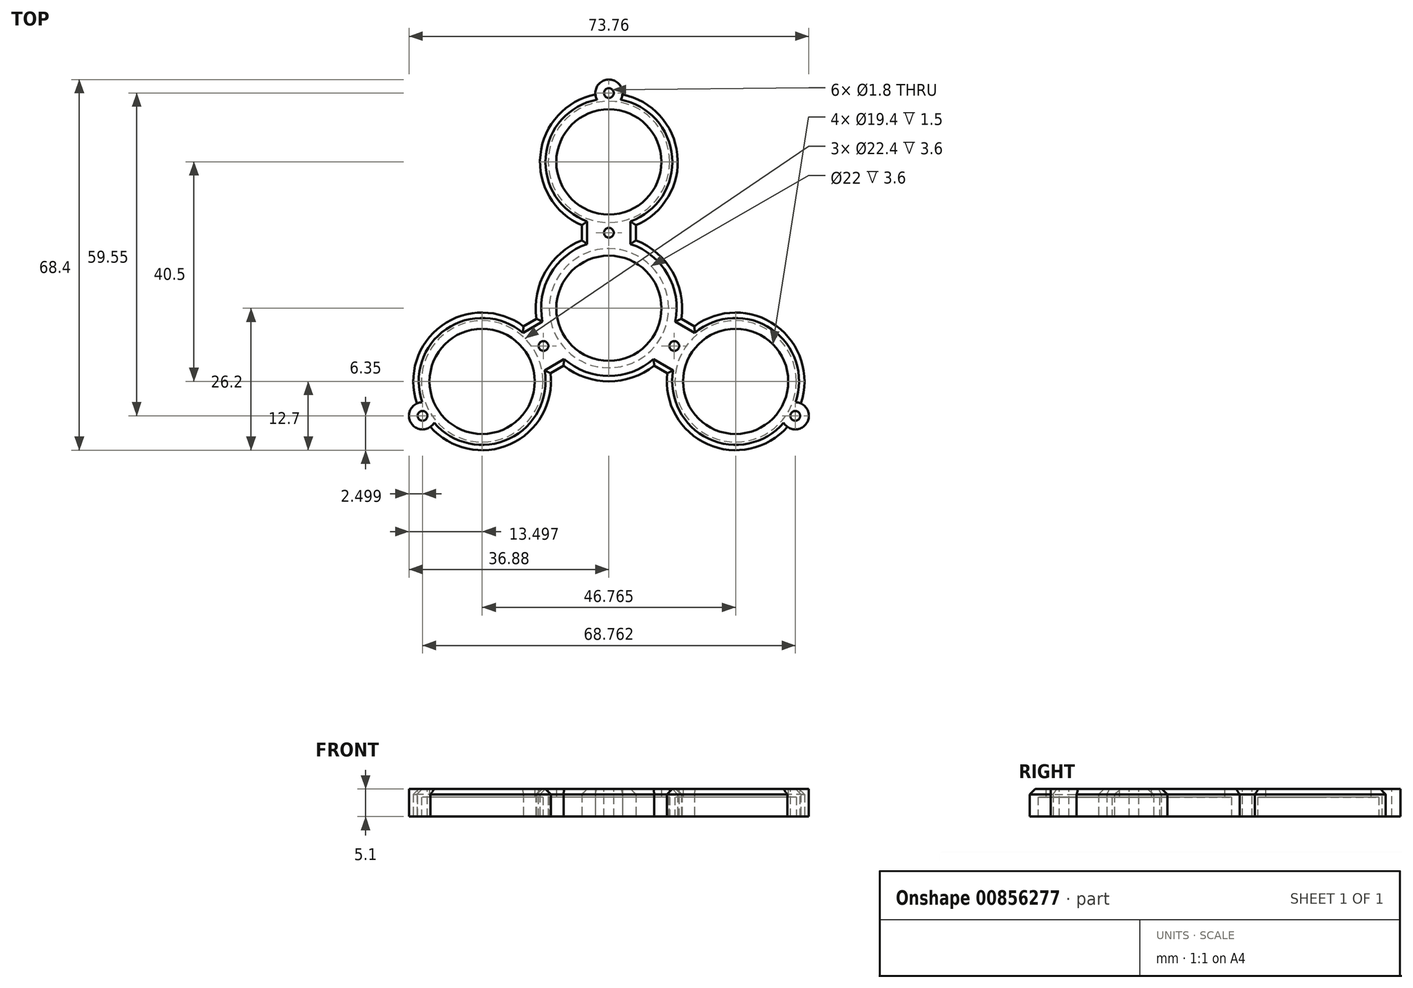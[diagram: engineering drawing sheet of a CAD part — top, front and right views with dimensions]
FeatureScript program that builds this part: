
annotation { "Feature Type Name" : "Feature", "Feature Type Description" : "" }
export const myFeature = defineFeature(function(context is Context, id is Id, definition is map)
    precondition{}
    {
        {
            var Q0;
            Q0=qCreatedBy(makeId("Top.planeOp"),FACE);
            var sketch = newSketch(context, id + "F0", { "sketchPlane" : qUnion([Q0])});
            skCircle(sketch, "E0", {"center": v(0, 0) * mm, "radius": 11 * mm});
            skCircle(sketch, "E1", {"center": v(0, 27) * mm, "radius": 11.2 * mm});
            skLineSegment(sketch, "E2", {"start": v(-5, 15.33) * mm, "end": v(-5, 12.54) * mm});
            skLineSegment(sketch, "E3", {"start": v(5, 15.33) * mm, "end": v(5, 12.54) * mm});
            skLineSegment(sketch, "E4", {"start": v(0, 27) * mm, "end": v(0, 13.5) * mm, "construction": true});
            skLineSegment(sketch, "E5", {"start": v(-5, 13.93) * mm, "end": v(0, 13.93) * mm, "construction": true});
            skLineSegment(sketch, "E6", {"start": v(0, 13.5) * mm, "end": v(0, 0) * mm, "construction": true});
            skLineSegment(sketch, "E7", {"start": v(0, 13.93) * mm, "end": v(5, 13.93) * mm, "construction": true});
            skArc(sketch, "E8", {"start": v(-2.49, 39.45) * mm, "mid": v(0, 37.2) * mm, "end": v(2.49, 39.45) * mm, "construction": true});
            skArc(sketch, "E9", {"start": v(2.49, 39.45) * mm, "mid": v(0, 42.2) * mm, "end": v(-2.49, 39.45) * mm});
            skArc(sketch, "E10", {"start": v(-2.49, 39.45) * mm, "mid": v(-12.63, 28.32) * mm, "end": v(-5, 15.33) * mm});
            skArc(sketch, "E11", {"start": v(-5, 15.33) * mm, "mid": v(0, 14.3) * mm, "end": v(5, 15.33) * mm, "construction": true});
            skArc(sketch, "E12", {"start": v(5, 15.33) * mm, "mid": v(12.63, 28.32) * mm, "end": v(2.49, 39.45) * mm});
            skArc(sketch, "E13", {"start": v(-5, 12.54) * mm, "mid": v(0, -13.5) * mm, "end": v(5, 12.54) * mm});
            skArc(sketch, "E14", {"start": v(5, 12.54) * mm, "mid": v(0, 13.5) * mm, "end": v(-5, 12.54) * mm, "construction": true});
            skArc(sketch, "E15.1.0", {"start": v(-35.41, -17.57) * mm, "mid": v(-36.55, -21.1) * mm, "end": v(-32.92, -21.88) * mm});
            skArc(sketch, "E15.1.1", {"start": v(-32.92, -21.88) * mm, "mid": v(-18.2, -25.1) * mm, "end": v(-10.77, -12) * mm});
            skLineSegment(sketch, "E15.1.2", {"start": v(-10.77, -12) * mm, "end": v(-8.36, -10.6) * mm});
            skArc(sketch, "E15.1.3", {"start": v(-15.77, -3.33) * mm, "mid": v(-30.84, -3.22) * mm, "end": v(-35.41, -17.57) * mm});
            skLineSegment(sketch, "E15.1.4", {"start": v(-15.77, -3.33) * mm, "end": v(-13.36, -1.94) * mm});
            skCircle(sketch, "E15.1.5", {"center": v(-23.38, -13.5) * mm, "radius": 11.2 * mm});
            skArc(sketch, "E15.2.0", {"start": v(32.92, -21.88) * mm, "mid": v(36.55, -21.1) * mm, "end": v(35.41, -17.57) * mm});
            skArc(sketch, "E15.2.1", {"start": v(35.41, -17.57) * mm, "mid": v(30.84, -3.22) * mm, "end": v(15.77, -3.33) * mm});
            skLineSegment(sketch, "E15.2.2", {"start": v(15.77, -3.33) * mm, "end": v(13.36, -1.94) * mm});
            skArc(sketch, "E15.2.3", {"start": v(10.77, -12) * mm, "mid": v(18.2, -25.1) * mm, "end": v(32.92, -21.88) * mm});
            skLineSegment(sketch, "E15.2.4", {"start": v(10.77, -12) * mm, "end": v(8.36, -10.6) * mm});
            skCircle(sketch, "E15.2.5", {"center": v(23.38, -13.5) * mm, "radius": 11.2 * mm});
            skSolve(sketch);
        }
        {
            var Q0;
            Q0=makeQuery(id+"F0.imprint","IMPRINT",FACE,{"disambiguationData":[TD([[makeQuery(id+"F0.imprint","IMPRINT",EDGE,{"derivedFrom":sQuery(id+"F0.wireOp",EDGE,"E0")}),-1.0]])]});
            var Q1;
            Q1=makeQuery(id+"F0.imprint","IMPRINT",FACE,{"disambiguationData":[TD([[makeQuery(id+"F0.imprint","IMPRINT",EDGE,{"derivedFrom":sQuery(id+"F0.wireOp",EDGE,"E15.1.0")}),1.0]])]});
            var Q2;
            Q2=makeQuery(id+"F0.imprint","IMPRINT",FACE,{"disambiguationData":[TD([[makeQuery(id+"F0.imprint","IMPRINT",EDGE,{"derivedFrom":sQuery(id+"F0.wireOp",EDGE,"E15.2.0")}),1.0]])]});
            extrude(context, id + "F1", {"entities" : qUnion([Q0, Q1, Q2]), "depth" : 3.6 * mm, "offsetDistance" : 25 * mm});
        }
        {
            var Q0;
            Q0=makeQuery(id+"F1.opExtrude","CAP_FACE",FACE,{"disambiguationData":[OSD([sQuery(id+"F0.wireOp",EDGE,"E0"),sQuery(id+"F0.wireOp",EDGE,"E1"),sQuery(id+"F0.wireOp",EDGE,"E2"),sQuery(id+"F0.wireOp",EDGE,"E3"),sQuery(id+"F0.wireOp",EDGE,"E9"),sQuery(id+"F0.wireOp",EDGE,"E10"),sQuery(id+"F0.wireOp",EDGE,"E12"),sQuery(id+"F0.wireOp",EDGE,"E13"),sQuery(id+"F0.wireOp",EDGE,"E15.1.0"),sQuery(id+"F0.wireOp",EDGE,"E15.1.1"),sQuery(id+"F0.wireOp",EDGE,"E15.1.2"),sQuery(id+"F0.wireOp",EDGE,"E15.1.3"),sQuery(id+"F0.wireOp",EDGE,"E15.1.4"),sQuery(id+"F0.wireOp",EDGE,"E15.1.5"),sQuery(id+"F0.wireOp",EDGE,"E15.2.0"),sQuery(id+"F0.wireOp",EDGE,"E15.2.1"),sQuery(id+"F0.wireOp",EDGE,"E15.2.2"),sQuery(id+"F0.wireOp",EDGE,"E15.2.3"),sQuery(id+"F0.wireOp",EDGE,"E15.2.4"),sQuery(id+"F0.wireOp",EDGE,"E15.2.5")])],"isStart":false});
            var sketch = newSketch(context, id + "F2", { "sketchPlane" : qUnion([Q0])});
            skCircle(sketch, "E16", {"center": v(0, 0) * mm, "radius": 9.7 * mm});
            skCircle(sketch, "E17", {"center": v(0, 27) * mm, "radius": 9.7 * mm});
            skCircle(sketch, "E18.1.0", {"center": v(-23.38, -13.5) * mm, "radius": 9.7 * mm});
            skCircle(sketch, "E18.2.0", {"center": v(23.38, -13.5) * mm, "radius": 9.7 * mm});
            skSolve(sketch);
        }
        {
            var Q0;
            Q0=makeQuery(id+"F2.imprint","IMPRINT",FACE,{"disambiguationData":[TD([[makeQuery(id+"F2.imprint","IMPRINT",EDGE,{"derivedFrom":sQuery(id+"F2.wireOp",EDGE,"E17")}),-1.0]])]});
            var Q1;
            Q1=makeQuery(id+"F2.imprint","IMPRINT",FACE,{"disambiguationData":[TD([[makeQuery(id+"F2.imprint","IMPRINT",EDGE,{"derivedFrom":makeQuery(id+"F1.opExtrude","CAP_EDGE",EDGE,{"disambiguationData":[OSD([sQuery(id+"F0.wireOp",EDGE,"E0")])],"isStart":false})}),-1.0]])]});
            var Q2;
            Q2=makeQuery(id+"F2.imprint","IMPRINT",FACE,{"disambiguationData":[TD([[makeQuery(id+"F2.imprint","IMPRINT",EDGE,{"derivedFrom":sQuery(id+"F2.wireOp",EDGE,"E18.1.0")}),-1.0]])]});
            var Q3;
            Q3=makeQuery(id+"F2.imprint","IMPRINT",FACE,{"disambiguationData":[TD([[makeQuery(id+"F2.imprint","IMPRINT",EDGE,{"derivedFrom":sQuery(id+"F2.wireOp",EDGE,"E18.2.0")}),-1.0]])]});
            var Q4;
            Q4=makeQuery(id+"F2.imprint","IMPRINT",FACE,{"disambiguationData":[TD([[makeQuery(id+"F2.imprint","IMPRINT",EDGE,{"derivedFrom":sQuery(id+"F2.wireOp",EDGE,"E16")}),-1.0]])]});
            extrude(context, id + "F3", {"entities" : qUnion([Q0, Q1, Q2, Q3, Q4]), "operationType" : NewBodyOperationType.ADD, "depth" : 1.5 * mm, "offsetDistance" : 25 * mm});
        }
        {
            var Q0;
            Q0=makeQuery(id+"F3.opExtrude","CAP_FACE",FACE,{"disambiguationData":[OSD([sQuery(id+"F0.wireOp",EDGE,"E0"),sQuery(id+"F0.wireOp",EDGE,"E2"),sQuery(id+"F0.wireOp",EDGE,"E3"),sQuery(id+"F0.wireOp",EDGE,"E9"),sQuery(id+"F0.wireOp",EDGE,"E10"),sQuery(id+"F0.wireOp",EDGE,"E12"),sQuery(id+"F0.wireOp",EDGE,"E13"),sQuery(id+"F0.wireOp",EDGE,"E15.1.0"),sQuery(id+"F0.wireOp",EDGE,"E15.1.1"),sQuery(id+"F0.wireOp",EDGE,"E15.1.2"),sQuery(id+"F0.wireOp",EDGE,"E15.1.3"),sQuery(id+"F0.wireOp",EDGE,"E15.1.4"),sQuery(id+"F0.wireOp",EDGE,"E15.2.0"),sQuery(id+"F0.wireOp",EDGE,"E15.2.1"),sQuery(id+"F0.wireOp",EDGE,"E15.2.2"),sQuery(id+"F0.wireOp",EDGE,"E15.2.3"),sQuery(id+"F0.wireOp",EDGE,"E15.2.4"),sQuery(id+"F2.wireOp",EDGE,"E17"),sQuery(id+"F2.wireOp",EDGE,"E18.1.0"),sQuery(id+"F2.wireOp",EDGE,"E18.2.0")])],"isStart":false});
            var sketch = newSketch(context, id + "F4", { "sketchPlane" : qUnion([Q0])});
            skCircle(sketch, "E19", {"center": v(0, 39.7) * mm, "radius": 1.8 * mm});
            skCircle(sketch, "E20", {"center": v(0, 13.93) * mm, "radius": 1.8 * mm});
            skPoint(sketch, "E20.centerSnap0", {"position": v(-5, 13.93) * mm});
            skCircle(sketch, "E21.1.0", {"center": v(-34.38, -19.85) * mm, "radius": 1.8 * mm});
            skCircle(sketch, "E21.1.1", {"center": v(-12.07, -6.97) * mm, "radius": 1.8 * mm});
            skCircle(sketch, "E21.2.0", {"center": v(34.38, -19.85) * mm, "radius": 1.8 * mm});
            skCircle(sketch, "E21.2.1", {"center": v(12.07, -6.97) * mm, "radius": 1.8 * mm});
            skPoint(sketch, "E21.center", {"position": v(0, 0) * mm});
            skSolve(sketch);
        }
        {
            var Q0;
            Q0=makeQuery(id+"F3.opExtrude","CAP_FACE",FACE,{"disambiguationData":[OSD([sQuery(id+"F0.wireOp",EDGE,"E2"),sQuery(id+"F0.wireOp",EDGE,"E3"),sQuery(id+"F0.wireOp",EDGE,"E9"),sQuery(id+"F0.wireOp",EDGE,"E10"),sQuery(id+"F0.wireOp",EDGE,"E12"),sQuery(id+"F0.wireOp",EDGE,"E13"),sQuery(id+"F0.wireOp",EDGE,"E15.1.0"),sQuery(id+"F0.wireOp",EDGE,"E15.1.1"),sQuery(id+"F0.wireOp",EDGE,"E15.1.2"),sQuery(id+"F0.wireOp",EDGE,"E15.1.3"),sQuery(id+"F0.wireOp",EDGE,"E15.1.4"),sQuery(id+"F0.wireOp",EDGE,"E15.2.0"),sQuery(id+"F0.wireOp",EDGE,"E15.2.1"),sQuery(id+"F0.wireOp",EDGE,"E15.2.2"),sQuery(id+"F0.wireOp",EDGE,"E15.2.3"),sQuery(id+"F0.wireOp",EDGE,"E15.2.4"),sQuery(id+"F2.wireOp",EDGE,"E16"),sQuery(id+"F2.wireOp",EDGE,"E17"),sQuery(id+"F2.wireOp",EDGE,"E18.1.0"),sQuery(id+"F2.wireOp",EDGE,"E18.2.0")])],"isStart":false});
            var sketch = newSketch(context, id + "F5", { "sketchPlane" : qUnion([Q0])});
            skCircle(sketch, "E22", {"center": v(0, 39.7) * mm, "radius": 0.9 * mm});
            skCircle(sketch, "E23", {"center": v(0, 13.93) * mm, "radius": 0.9 * mm});
            skCircle(sketch, "E24.1.0", {"center": v(-34.38, -19.85) * mm, "radius": 0.9 * mm});
            skCircle(sketch, "E24.1.1", {"center": v(-12.07, -6.97) * mm, "radius": 0.9 * mm});
            skCircle(sketch, "E24.2.0", {"center": v(34.38, -19.85) * mm, "radius": 0.9 * mm});
            skCircle(sketch, "E24.2.1", {"center": v(12.07, -6.97) * mm, "radius": 0.9 * mm});
            skPoint(sketch, "E24.center", {"position": v(0, 0) * mm});
            skSolve(sketch);
        }
        {
            var Q0;
            Q0=makeQuery(id+"F5.imprint","IMPRINT",FACE,{"disambiguationData":[TD([[makeQuery(id+"F5.imprint","IMPRINT",EDGE,{"derivedFrom":sQuery(id+"F5.wireOp",EDGE,"E22")}),1.0]])]});
            var Q1;
            Q1=makeQuery(id+"F5.imprint","IMPRINT",FACE,{"disambiguationData":[TD([[makeQuery(id+"F5.imprint","IMPRINT",EDGE,{"derivedFrom":sQuery(id+"F5.wireOp",EDGE,"E23")}),1.0]])]});
            var Q2;
            Q2=makeQuery(id+"F5.imprint","IMPRINT",FACE,{"disambiguationData":[TD([[makeQuery(id+"F5.imprint","IMPRINT",EDGE,{"derivedFrom":sQuery(id+"F5.wireOp",EDGE,"E24.1.1")}),1.0]])]});
            var Q3;
            Q3=makeQuery(id+"F5.imprint","IMPRINT",FACE,{"disambiguationData":[TD([[makeQuery(id+"F5.imprint","IMPRINT",EDGE,{"derivedFrom":sQuery(id+"F5.wireOp",EDGE,"E24.1.0")}),1.0]])]});
            var Q4;
            Q4=makeQuery(id+"F5.imprint","IMPRINT",FACE,{"disambiguationData":[TD([[makeQuery(id+"F5.imprint","IMPRINT",EDGE,{"derivedFrom":sQuery(id+"F5.wireOp",EDGE,"E24.2.1")}),1.0]])]});
            var Q5;
            Q5=makeQuery(id+"F5.imprint","IMPRINT",FACE,{"disambiguationData":[TD([[makeQuery(id+"F5.imprint","IMPRINT",EDGE,{"derivedFrom":sQuery(id+"F5.wireOp",EDGE,"E24.2.0")}),1.0]])]});
            var Q6;
            Q6=makeQuery(id+"F1.opExtrude","CAP_FACE",FACE,{"disambiguationData":[OSD([sQuery(id+"F0.wireOp",EDGE,"E0"),sQuery(id+"F0.wireOp",EDGE,"E1"),sQuery(id+"F0.wireOp",EDGE,"E2"),sQuery(id+"F0.wireOp",EDGE,"E3"),sQuery(id+"F0.wireOp",EDGE,"E9"),sQuery(id+"F0.wireOp",EDGE,"E10"),sQuery(id+"F0.wireOp",EDGE,"E12"),sQuery(id+"F0.wireOp",EDGE,"E13"),sQuery(id+"F0.wireOp",EDGE,"E15.1.0"),sQuery(id+"F0.wireOp",EDGE,"E15.1.1"),sQuery(id+"F0.wireOp",EDGE,"E15.1.2"),sQuery(id+"F0.wireOp",EDGE,"E15.1.3"),sQuery(id+"F0.wireOp",EDGE,"E15.1.4"),sQuery(id+"F0.wireOp",EDGE,"E15.1.5"),sQuery(id+"F0.wireOp",EDGE,"E15.2.0"),sQuery(id+"F0.wireOp",EDGE,"E15.2.1"),sQuery(id+"F0.wireOp",EDGE,"E15.2.2"),sQuery(id+"F0.wireOp",EDGE,"E15.2.3"),sQuery(id+"F0.wireOp",EDGE,"E15.2.4"),sQuery(id+"F0.wireOp",EDGE,"E15.2.5")])],"isStart":true});
            extrude(context, id + "F6", {"entities" : qUnion([Q0, Q1, Q2, Q3, Q4, Q5]), "operationType" : NewBodyOperationType.REMOVE, "endBound" : BoundingType.UP_TO_SURFACE, "oppositeDirection" : true, "depth" : 25 * mm, "endBoundEntityFace" : qUnion([Q6]), "offsetDistance" : 25 * mm});
        }
        {
            var Q0;
            Q0=makeQuery(id+"F3.opExtrude","CAP_EDGE",EDGE,{"disambiguationData":[OSD([sQuery(id+"F0.wireOp",EDGE,"E15.1.1")])],"isStart":false});
            var Q1;
            Q1=makeQuery(id+"F3.opExtrude","CAP_EDGE",EDGE,{"disambiguationData":[OSD([sQuery(id+"F0.wireOp",EDGE,"E15.1.2")])],"isStart":false});
            var Q2;
            {var subQ0=sQuery(id+"F0.wireOp",EDGE,"E13");Q2=makeQuery(id+"F3.opExtrude","CAP_EDGE",EDGE,{"disambiguationData":[OSD([subQ0]),TDD([makeQuery(id+"F2.imprint","IMPRINT",EDGE,{"derivedFrom":makeQuery(id+"F1.opExtrude","CAP_EDGE",EDGE,{"disambiguationData":[OSD([subQ0]),TDD([makeQuery(id+"F0.imprint","IMPRINT",EDGE,{"disambiguationData":[TD([[makeQuery(id+"F0.imprint","INTERSECT",VERTEX,{"derivedFrom":[subQ0,sQuery(id+"F0.wireOp",EDGE,"E15.1.2")]}),-1.0]])],"derivedFrom":subQ0})])],"isStart":false})})])],"isStart":false});}
            var Q3;
            Q3=makeQuery(id+"F3.opExtrude","CAP_EDGE",EDGE,{"disambiguationData":[OSD([sQuery(id+"F0.wireOp",EDGE,"E15.2.4")])],"isStart":false});
            var Q4;
            Q4=makeQuery(id+"F3.opExtrude","CAP_EDGE",EDGE,{"disambiguationData":[OSD([sQuery(id+"F0.wireOp",EDGE,"E15.2.3")])],"isStart":false});
            var Q5;
            Q5=makeQuery(id+"F3.opExtrude","CAP_EDGE",EDGE,{"disambiguationData":[OSD([sQuery(id+"F0.wireOp",EDGE,"E15.2.1")])],"isStart":false});
            var Q6;
            Q6=makeQuery(id+"F3.opExtrude","CAP_EDGE",EDGE,{"disambiguationData":[OSD([sQuery(id+"F0.wireOp",EDGE,"E15.2.2")])],"isStart":false});
            var Q7;
            {var subQ0=sQuery(id+"F0.wireOp",EDGE,"E13");Q7=makeQuery(id+"F3.opExtrude","CAP_EDGE",EDGE,{"disambiguationData":[OSD([subQ0]),TDD([makeQuery(id+"F2.imprint","IMPRINT",EDGE,{"derivedFrom":makeQuery(id+"F1.opExtrude","CAP_EDGE",EDGE,{"disambiguationData":[OSD([subQ0]),TDD([makeQuery(id+"F0.imprint","IMPRINT",EDGE,{"disambiguationData":[TD([[makeQuery(id+"F0.imprint","INTERSECT",VERTEX,{"derivedFrom":[sQuery(id+"F0.wireOp",EDGE,"E3"),subQ0]}),1.0]])],"derivedFrom":subQ0})])],"isStart":false})})])],"isStart":false});}
            var Q8;
            Q8=makeQuery(id+"F3.opExtrude","CAP_EDGE",EDGE,{"disambiguationData":[OSD([sQuery(id+"F0.wireOp",EDGE,"E3")])],"isStart":false});
            var Q9;
            Q9=makeQuery(id+"F3.opExtrude","CAP_EDGE",EDGE,{"disambiguationData":[OSD([sQuery(id+"F0.wireOp",EDGE,"E12")])],"isStart":false});
            var Q10;
            Q10=makeQuery(id+"F3.opExtrude","CAP_EDGE",EDGE,{"disambiguationData":[OSD([sQuery(id+"F0.wireOp",EDGE,"E10")])],"isStart":false});
            var Q11;
            Q11=makeQuery(id+"F3.opExtrude","CAP_EDGE",EDGE,{"disambiguationData":[OSD([sQuery(id+"F0.wireOp",EDGE,"E2")])],"isStart":false});
            var Q12;
            {var subQ0=sQuery(id+"F0.wireOp",EDGE,"E13");Q12=makeQuery(id+"F3.opExtrude","CAP_EDGE",EDGE,{"disambiguationData":[OSD([subQ0]),TDD([makeQuery(id+"F2.imprint","IMPRINT",EDGE,{"derivedFrom":makeQuery(id+"F1.opExtrude","CAP_EDGE",EDGE,{"disambiguationData":[OSD([subQ0]),TDD([makeQuery(id+"F0.imprint","IMPRINT",EDGE,{"disambiguationData":[TD([[makeQuery(id+"F0.imprint","INTERSECT",VERTEX,{"derivedFrom":[sQuery(id+"F0.wireOp",EDGE,"E2"),subQ0]}),-1.0]])],"derivedFrom":subQ0})])],"isStart":false})})])],"isStart":false});}
            var Q13;
            Q13=makeQuery(id+"F3.opExtrude","CAP_EDGE",EDGE,{"disambiguationData":[OSD([sQuery(id+"F0.wireOp",EDGE,"E15.1.4")])],"isStart":false});
            var Q14;
            Q14=makeQuery(id+"F3.opExtrude","CAP_EDGE",EDGE,{"disambiguationData":[OSD([sQuery(id+"F0.wireOp",EDGE,"E15.1.3")])],"isStart":false});
            chamfer(context, id + "F7", {"entities" : qUnion([Q0, Q1, Q2, Q3, Q4, Q5, Q6, Q7, Q8, Q9, Q10, Q11, Q12, Q13, Q14]), "width" : 1 * mm, "tangentPropagation" : true});
        }
    });
